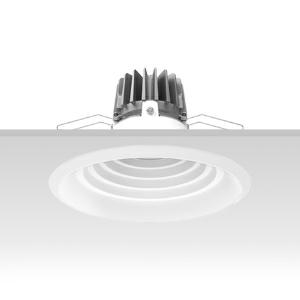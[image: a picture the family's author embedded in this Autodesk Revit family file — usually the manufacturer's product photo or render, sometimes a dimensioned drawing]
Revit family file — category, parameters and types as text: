
# Revit family: 3f_filippi_-_3f_reno_bianco_ugr_3f_filippi_-_30757_-_3f_reno_200_wh_2000-930_dali_ugr
name_source: partatom
category: Lighting Fixtures
units: mm (PartAtom-declared; Revit-internal decimal feet)

## family parameters
Cut with Voids When Loaded = No
Host = Face
Light Source = No
Part Type = Normal
Room Calculation Point = No
Round Connector Dimension = Use Diameter
Shared = No

## types (1)
- 3F Filippi - 3F Reno Bianco UGR (1 x LED, 2354 lm, 24 W, 3000 K)
    Apparent Load = 24 VA
    Approval mark = CE
    CIE Flux Codes = 90 100 100 100 100
    Color Rendering = 90
    Color Temperature = 3000 K
    Control Gear = Electronic transformer
    Default Elevation = 1800 mm
    Description = ILLUMINOTECHNICAL
Luminous efficiency 100% (DLOR 100%, ULOR 0%).
Initial luminous flux of the luminaire 2354 lm.
Direct symmetric UGR distribution.
Installation Interdistance Transv.D = 0.99 x hu - Long.D = 1.01 x hu.
Average luminance <500 cd/m² for radial angles >65°.
Tabular UGR (CIE 117 - 4H-8H; S=0.25H; 70/50/20): RUG 17.2 - 17.2.
Beam angle: 64° - 65°.
Luminous efficacy 98 lm/W.
Lifetime (L90/B10): 30000 h. (tq+25°C)
Lifetime (L85/B10): 50000 h. (tq+25°C)
Lifetime (L70/B10): 80000 h. (tq+25°C)
Sudden decreased luminous flux after 50000 hours: 0% (C0).
Photobiological safety in compliance with IEC/TR 62778: RG0 risk exempt, (IEC 62471).
In compliance with IEC/EN 62722-2-1 - IEC/EN 62717 standards.

SOURCE
Compact LED module 2000/930.
Energy efficiency class (UE 2019/2020 - UE 2019/2015): F.
CIE 13.3 Colour rendering index: CRI >90 (R9 >50%).
IES TM-30 Fidelity Index: Rf = 92 Rg = 101.
CCT nominal colour temperature 3000 K.
Colour initial tolerance (MacAdam): SDCM 3.
Zhaga Book 3 compliant.

MECHANICAL
Passive heat dissipator in die-casting aluminium, oversized, for optimum thermal management of the LED module.
Parabolic element with graduated/concentric rings in white polycarbonate.
Internal specular metallic louvre to optimise control of the luminous flux in polycarbonate.
Transparent external lens with glossy and satin differentiated surfaces, with a cooling and anti-insect system in methacrylate (PMMA).
Fastening spring clips in stainless steel.
Dimensions: diameter 216 mm, height 142 mm. Weight 0.925 kg.
IP44 protection degree for exposed part, IP20 for recessed part.
Mechanical strength to impacts IK04 (0.5 joule).
Glow-wire test resistance 650°C.

ELECTRICAL
Wiring on a separate unit.
Halogen Free DALI-2 DATI (Parts 251, 252, 253), PUSH-DIM, electronic wiring 230V-50/60Hz, power factor 0.95 at full load, THD <25%, constant output current, SELV, class II, 1 driver, 1 DALI addresse.
Power of the luminaire 24 W.
ENEC - CE.
SAFE FLICKER: PstLM=<1 and SVM=<0.4 (IEC TR 61547-1 and IEC TR 63158), to ensure a more comfortable and safe light.
Luminaire compliant with EN 60598-2-22 for power supply from a centralised emergency system CPSS (Central Power Supply System), not incorporated in the luminaire - high risk areas excluded. The default power and flux are 100% in AC and 100% in DC.
Ambient temperature from 0°C to +25°C.
Temperature class T6 max 85°C.
Relative humidity UR: <85%.

INSTALLATION
Pull-up recessed fitting.
False ceiling carving: 200 mm.
All accessories dedicated to this product are available on the Catalog and on our website www.3F-Filippi.com.

APPLICATIONS
In environments with VDTs, managerial offices and staterooms, public offices and schools.
In false ceilings with narrow voids.

LIGHT MANAGEMENT
Recommended minimum setting: 10%.
The luminaire, equipped with (DALI-2 DATI) driver, can be controlled manually with 3F Easy Dim technology or automatically/manually with wired or wireless DALI/D2D control systems.
The D2D driver guarantees interoperability with other devices with the same certification by making the following information available:
Device Data (Part 251), Energy Report (Part 252), Diagnosis & Maintenance (Part 253).
In electrical systems without a regulation system (manual or automatic) and DALI bus, a suitable jumper must be made on the DA-DA terminals of the appliance.

WARNING
Luminaire designed for disposal/recycling at end-of-life.
Replaceable (LED only) light source by a professional. Replaceable control gear by a professional.
    Height = 0 mm  [stored 0 ft]
    Lamp = 1 x LED
    Lamp Light Flux = 2354 lm
    Lamp Power = 24 W
    Lamp count = 1
    Length = 216 mm
    Lifetime = 50000 h
    Luminous efficacy = 98 lm/W
    Manufacturer = 3F Filippi
    ModVariant = No
    Model = 3F Filippi - 30757 - 3F Reno 200 WH 2000-930 DALI UGR
    Mounting Place = Ceiling
    Mounting Type = Recessed
    Number of Poles = 1
    OnlyDefault = Yes
    Power Factor = 1
    Product Name = 3F Filippi - 3F Reno Bianco UGR
    Product group = recessed luminaire
    ProductGroupID = 4
    Protection Class = Protection class II
    Protection Degree = IP 20
    RLX_Detail_Level = 1
    RLX_Emergency_Light_Flux = 0 lm
    RLX_Emergency_Type = 0
    RLX_Emergency_Type_DB = No
    RlxData = <blob elided: 90177 chars, md5=cd2e68cd>
    Socket = socket
    Standby Power = 0 W
    System Light Flux = 2354 lm
    System Power = 24 W
    Type Comments = Product without accessories
    Type Image = 3ffilippi_3f_reno_200_wh_2000.jpg
    URL = http://relux.com
    VarID = ---
    Voltage = 0 V
    Weight = 0.00 kg
    Width = 0 mm  [stored 0 ft]

note: [stored X ft] marks values corroborated as IEEE doubles in the binary element streams (Revit-internal decimal feet)

## geometry (parser evidence)
native form markers: Blend x4, Sweep x10
no freeform markers — native parametric forms only
